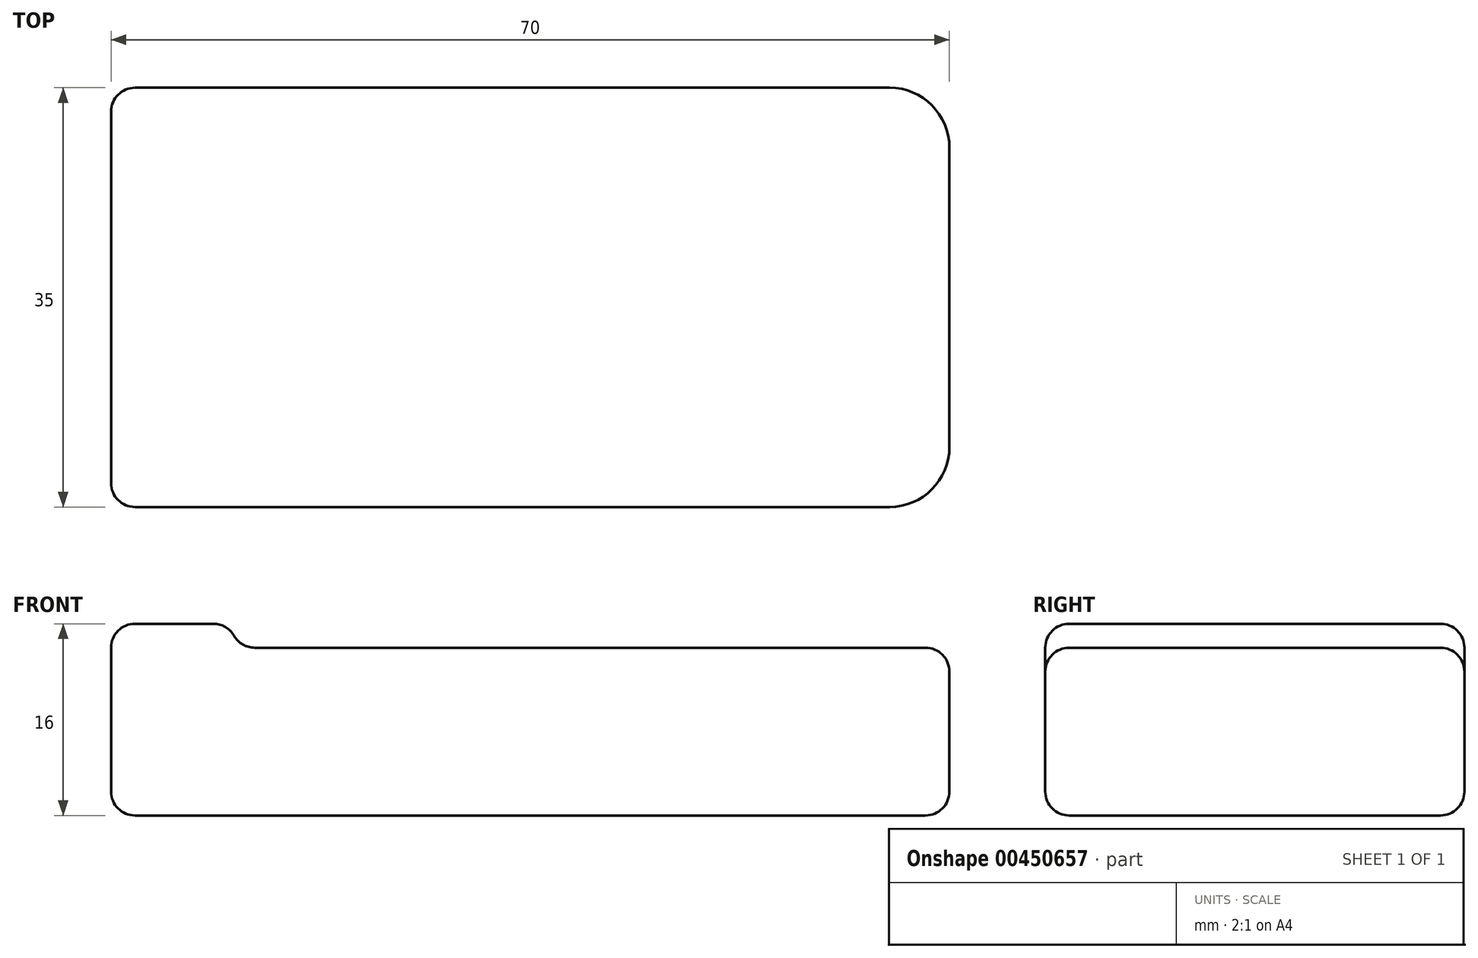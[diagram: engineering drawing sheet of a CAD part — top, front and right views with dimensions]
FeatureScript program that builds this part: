
annotation { "Feature Type Name" : "Feature", "Feature Type Description" : "" }
export const myFeature = defineFeature(function(context is Context, id is Id, definition is map)
    precondition{}
    {
        {
            var Q0;
            Q0=qCreatedBy(makeId("Front.planeOp"),FACE);
            var sketch = newSketch(context, id + "F0", { "sketchPlane" : qUnion([Q0])});
            skLineSegment(sketch, "E0", {"start": v(-29.83, 3.74) * mm, "end": v(-29.83, -12.26) * mm});
            skLineSegment(sketch, "E1", {"start": v(-29.83, -12.26) * mm, "end": v(40.17, -12.26) * mm});
            skLineSegment(sketch, "E2", {"start": v(40.17, -12.26) * mm, "end": v(40.17, 1.74) * mm});
            skLineSegment(sketch, "E3", {"start": v(40.17, 1.74) * mm, "end": v(-17.83, 1.74) * mm});
            skLineSegment(sketch, "E4", {"start": v(-19.83, 3.74) * mm, "end": v(-19.83, 3.74) * mm});
            skLineSegment(sketch, "E5", {"start": v(-19.83, 3.74) * mm, "end": v(-29.83, 3.74) * mm});
            skPoint(sketch, "E6.visualSharp", {"position": v(-19.83, 1.74) * mm});
            skArc(sketch, "E6.filletArc", {"start": v(-19.83, 3.74) * mm, "mid": v(-19.24, 2.33) * mm, "end": v(-17.83, 1.74) * mm});
            skSolve(sketch);
        }
        {
            var Q0;
            Q0=makeQuery(id+"F0.imprint","IMPRINT",FACE,{"disambiguationData":[TD([[makeQuery(id+"F0.imprint","IMPRINT",EDGE,{"derivedFrom":sQuery(id+"F0.wireOp",EDGE,"E0")}),1.0]])]});
            extrude(context, id + "F1", {"entities" : qUnion([Q0]), "depth" : 35 * mm});
        }
        {
            var Q0;
            Q0=makeQuery(id+"F1.opExtrude","CAP_EDGE",EDGE,{"disambiguationData":[OSD([sQuery(id+"F0.wireOp",EDGE,"E2")])],"isStart":false});
            var Q1;
            Q1=makeQuery(id+"F1.opExtrude","CAP_EDGE",EDGE,{"disambiguationData":[OSD([sQuery(id+"F0.wireOp",EDGE,"E2")])],"isStart":true});
            fillet(context, id + "F2", {"entities" : qUnion([Q0, Q1]), "radius" : 5 * mm, "tangentPropagation" : true, "allowEdgeOverflow" : false});
        }
        {
            var Q0;
            Q0=makeQuery(id+"F1.opExtrude","SWEPT_FACE",FACE,{"disambiguationData":[OSD([sQuery(id+"F0.wireOp",EDGE,"E5")])]});
            var Q1;
            Q1=makeQuery(id+"F1.opExtrude","CAP_FACE",FACE,{"disambiguationData":[OSD([sQuery(id+"F0.wireOp",EDGE,"E0"),sQuery(id+"F0.wireOp",EDGE,"E1"),sQuery(id+"F0.wireOp",EDGE,"E2"),sQuery(id+"F0.wireOp",EDGE,"E3"),sQuery(id+"F0.wireOp",EDGE,"E4"),sQuery(id+"F0.wireOp",EDGE,"E5")])],"isStart":false});
            var Q2;
            Q2=makeQuery(id+"F1.opExtrude","CAP_FACE",FACE,{"disambiguationData":[OSD([sQuery(id+"F0.wireOp",EDGE,"E0"),sQuery(id+"F0.wireOp",EDGE,"E1"),sQuery(id+"F0.wireOp",EDGE,"E2"),sQuery(id+"F0.wireOp",EDGE,"E3"),sQuery(id+"F0.wireOp",EDGE,"E4"),sQuery(id+"F0.wireOp",EDGE,"E5")])],"isStart":true});
            var Q3;
            Q3=makeQuery(id+"F1.opExtrude","SWEPT_FACE",FACE,{"disambiguationData":[OSD([sQuery(id+"F0.wireOp",EDGE,"E0")])]});
            fillet(context, id + "F3", {"entities" : qUnion([Q0, Q1, Q2, Q3]), "radius" : 2 * mm, "tangentPropagation" : true, "allowEdgeOverflow" : false});
        }
        {
            var Q0;
            Q0=makeQuery(id+"F1.opExtrude","SWEPT_FACE",FACE,{"disambiguationData":[OSD([sQuery(id+"F0.wireOp",EDGE,"E3")])]});
            cPlane(context, id + "F4", {"entities" : qUnion([Q0]), "cplaneType" : CPlaneType.OFFSET, "offset" : 0 * mm, "width" : 150 * mm, "height" : 150 * mm});
        }
    });
